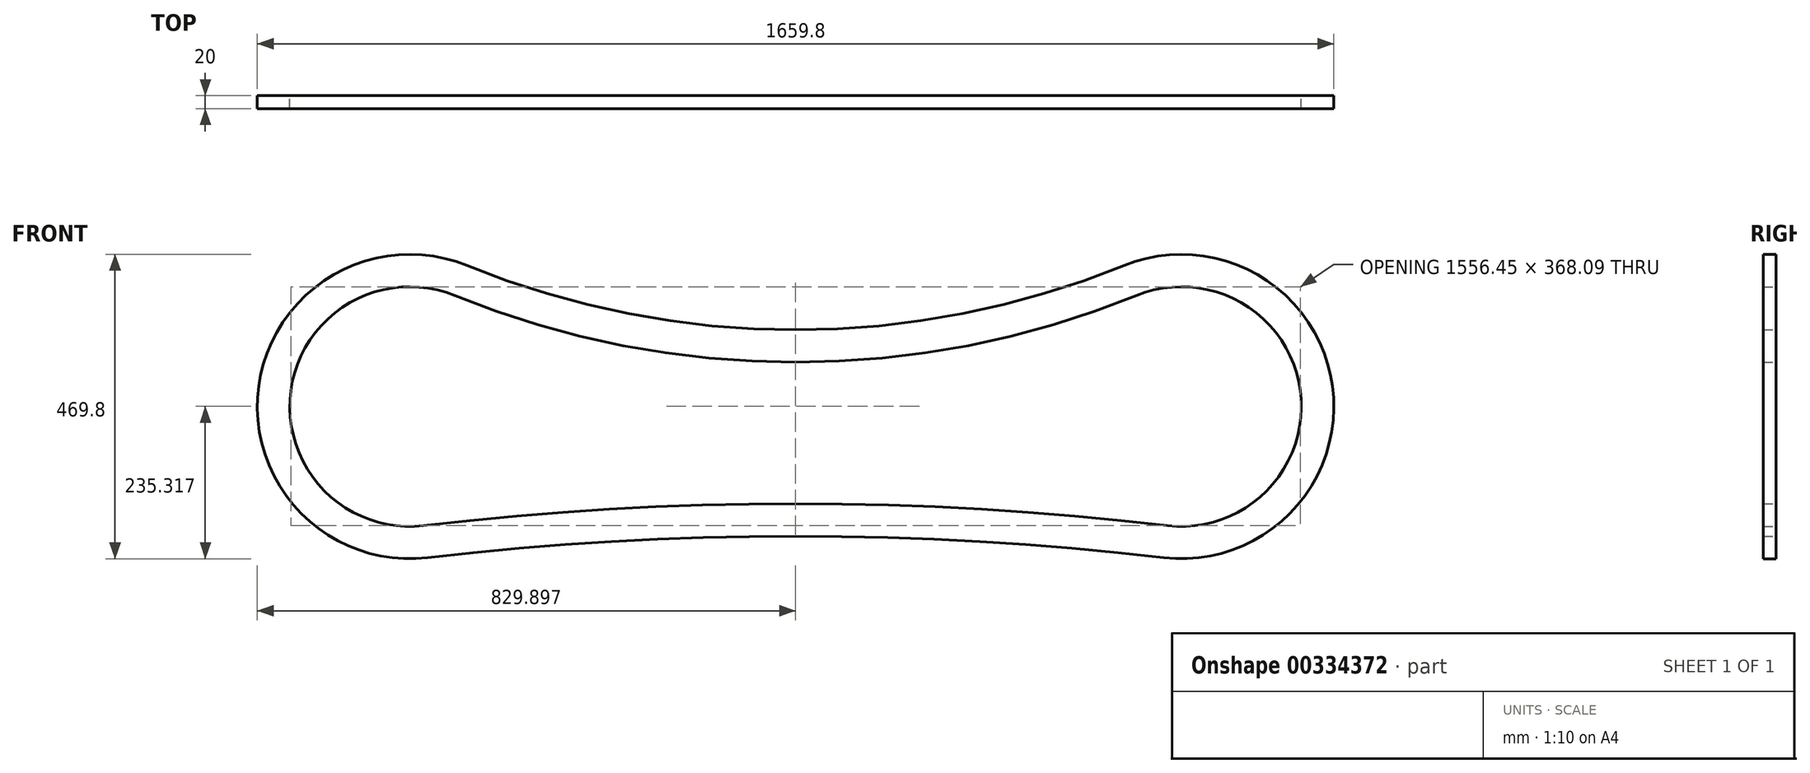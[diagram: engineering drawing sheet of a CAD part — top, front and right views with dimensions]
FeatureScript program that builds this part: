
annotation { "Feature Type Name" : "Feature", "Feature Type Description" : "" }
export const myFeature = defineFeature(function(context is Context, id is Id, definition is map)
    precondition{}
    {
        {
            var Q0;
            Q0=qCreatedBy(makeId("Front.planeOp"),FACE);
            var sketch = newSketch(context, id + "F0", { "sketchPlane" : qUnion([Q0])});
            skArc(sketch, "E0", {"start": v(-507.3, 230.25) * mm, "mid": v(-828.64, 44.23) * mm, "end": v(-568.38, -220.6) * mm});
            skArc(sketch, "E1", {"start": v(566.65, -220.6) * mm, "mid": v(826.9, 44.23) * mm, "end": v(505.57, 230.25) * mm});
            skArc(sketch, "E2", {"start": v(566.65, -220.6) * mm, "mid": v(-0.86, -187.28) * mm, "end": v(-568.38, -220.6) * mm});
            skPoint(sketch, "E2.centerSnap0", {"position": v(-0.86, 12.7) * mm});
            skArc(sketch, "E3", {"start": v(-507.3, 230.25) * mm, "mid": v(-0.86, 131.12) * mm, "end": v(505.57, 230.25) * mm});
            skArc(sketch, "E4.0", {"start": v(-526.14, 183.94) * mm, "mid": v(-779.09, 37.52) * mm, "end": v(-574.23, -170.94) * mm});
            skArc(sketch, "E4.1", {"start": v(-526.14, 183.94) * mm, "mid": v(-0.86, 81.12) * mm, "end": v(524.42, 183.94) * mm});
            skArc(sketch, "E4.2", {"start": v(572.5, -170.94) * mm, "mid": v(777.36, 37.52) * mm, "end": v(524.42, 183.94) * mm});
            skArc(sketch, "E4.3", {"start": v(572.5, -170.94) * mm, "mid": v(-0.86, -137.28) * mm, "end": v(-574.23, -170.94) * mm});
            skSolve(sketch);
        }
        {
            var Q0;
            Q0=makeQuery(id+"F0.imprint","IMPRINT",FACE,{"disambiguationData":[TD([[makeQuery(id+"F0.imprint","IMPRINT",EDGE,{"derivedFrom":sQuery(id+"F0.wireOp",EDGE,"E0")}),1.0]])]});
            extrude(context, id + "F1", {"entities" : qUnion([Q0]), "depth" : 20 * mm});
        }
    });
